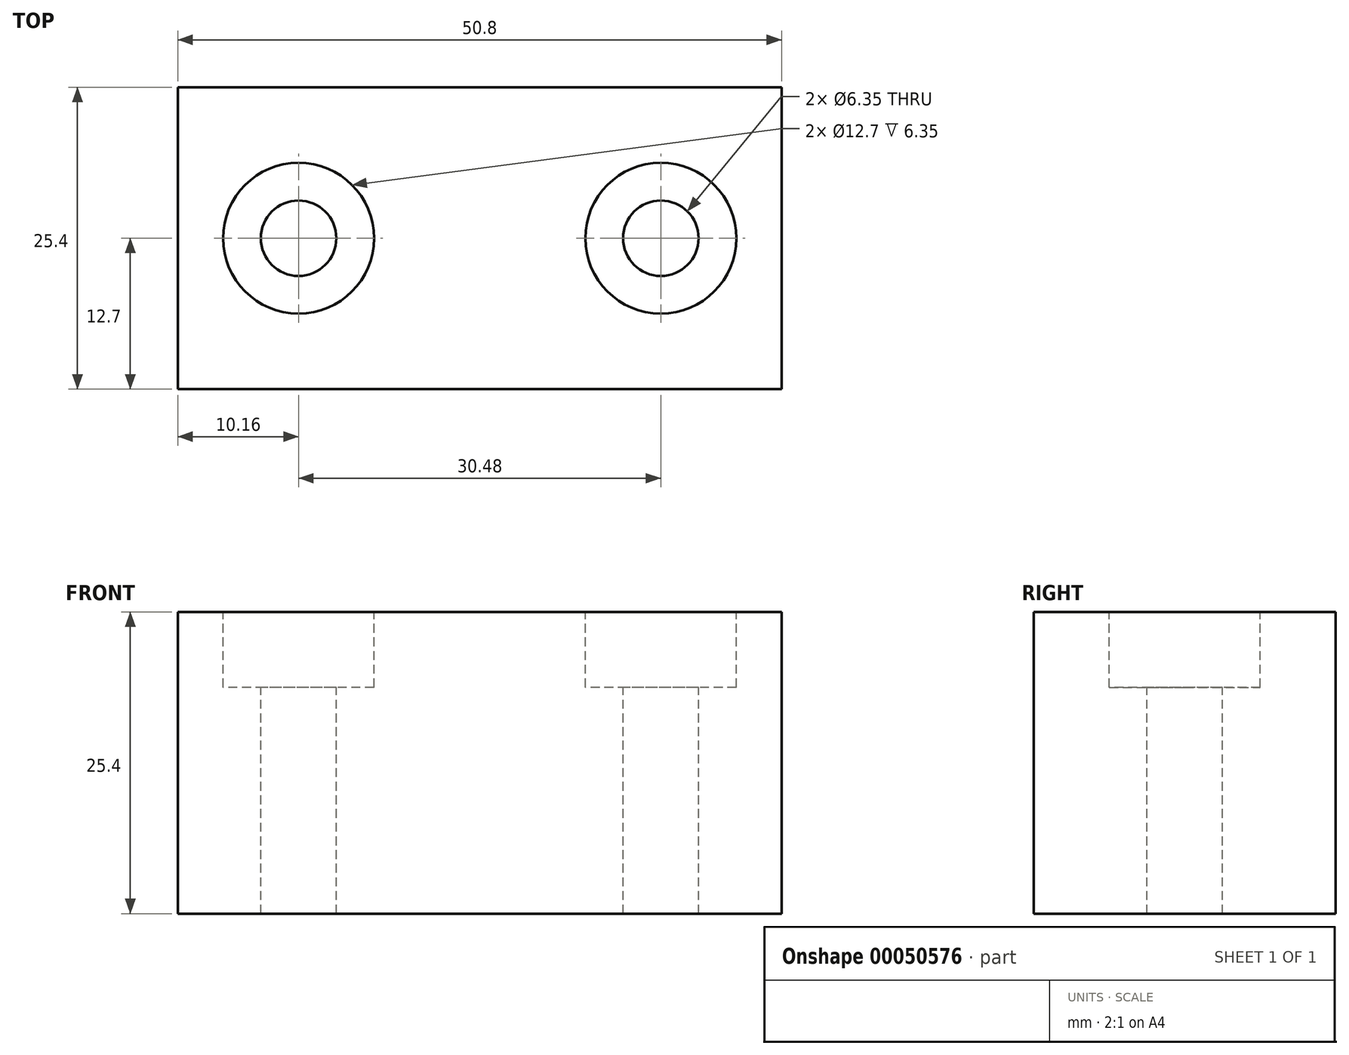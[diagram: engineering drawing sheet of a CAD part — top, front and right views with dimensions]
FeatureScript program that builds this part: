
annotation { "Feature Type Name" : "Feature", "Feature Type Description" : "" }
export const myFeature = defineFeature(function(context is Context, id is Id, definition is map)
    precondition{}
    {
        {
            var Q0;
            Q0=qCreatedBy(makeId("Top.planeOp"),FACE);
            var sketch = newSketch(context, id + "F0", { "sketchPlane" : qUnion([Q0])});
            skLineSegment(sketch, "E0.rect.bottom", {"start": v(25.4, -12.7) * mm, "end": v(-25.4, -12.7) * mm});
            skLineSegment(sketch, "E0.rect.top", {"start": v(25.4, 12.7) * mm, "end": v(-25.4, 12.7) * mm});
            skLineSegment(sketch, "E0.rect.left", {"start": v(25.4, -12.7) * mm, "end": v(25.4, 12.7) * mm});
            skLineSegment(sketch, "E0.rect.right", {"start": v(-25.4, -12.7) * mm, "end": v(-25.4, 12.7) * mm});
            skPoint(sketch, "E0.rect.middle", {"position": v(0, 0) * mm});
            skSolve(sketch);
        }
        {
            var Q0;
            Q0=makeQuery(id+"F0.imprint","IMPRINT",FACE,{"disambiguationData":[TD([[makeQuery(id+"F0.imprint","IMPRINT",EDGE,{"derivedFrom":sQuery(id+"F0.wireOp",EDGE,"E0.rect.bottom")}),-1.0]])]});
            extrude(context, id + "F1", {"entities" : qUnion([Q0]), "endBound" : BoundingType.SYMMETRIC, "depth" : 25.4 * mm});
        }
        {
            var Q0;
            Q0=makeQuery(id+"F1.opExtrude","CAP_FACE",FACE,{"disambiguationData":[OSD([sQuery(id+"F0.wireOp",EDGE,"E0.rect.bottom"),sQuery(id+"F0.wireOp",EDGE,"E0.rect.top"),sQuery(id+"F0.wireOp",EDGE,"E0.rect.left"),sQuery(id+"F0.wireOp",EDGE,"E0.rect.right")])],"isStart":false});
            var sketch = newSketch(context, id + "F2", { "sketchPlane" : qUnion([Q0])});
            skLineSegment(sketch, "E1", {"start": v(-15.24, 0) * mm, "end": v(15.24, 0) * mm});
            skSolve(sketch);
        }
        {
            var Q0;
            Q0=sQuery(id+"F2.wireOp",VERTEX,"E1.start");
            var Q1;
            Q1=sQuery(id+"F2.wireOp",VERTEX,"E1.end");
            var Q2;
            Q2=makeQuery(id+"F1.opExtrude","SWEPT_BODY",BODY,{"disambiguationData":[OSD([sQuery(id+"F0.wireOp",EDGE,"E0.rect.bottom"),sQuery(id+"F0.wireOp",EDGE,"E0.rect.top"),sQuery(id+"F0.wireOp",EDGE,"E0.rect.left"),sQuery(id+"F0.wireOp",EDGE,"E0.rect.right")])]});
            hole(context, id + "F3", {"style" : HoleStyle.C_BORE, "holeDiameter" : 6.35 * mm, "cBoreDiameter" : 12.7 * mm, "cBoreDepth" : 6.35 * mm, "endStyle" : HoleEndStyle.THROUGH, "locations" : qUnion([Q0, Q1]), "scope" : qUnion([Q2])});
        }
    });
